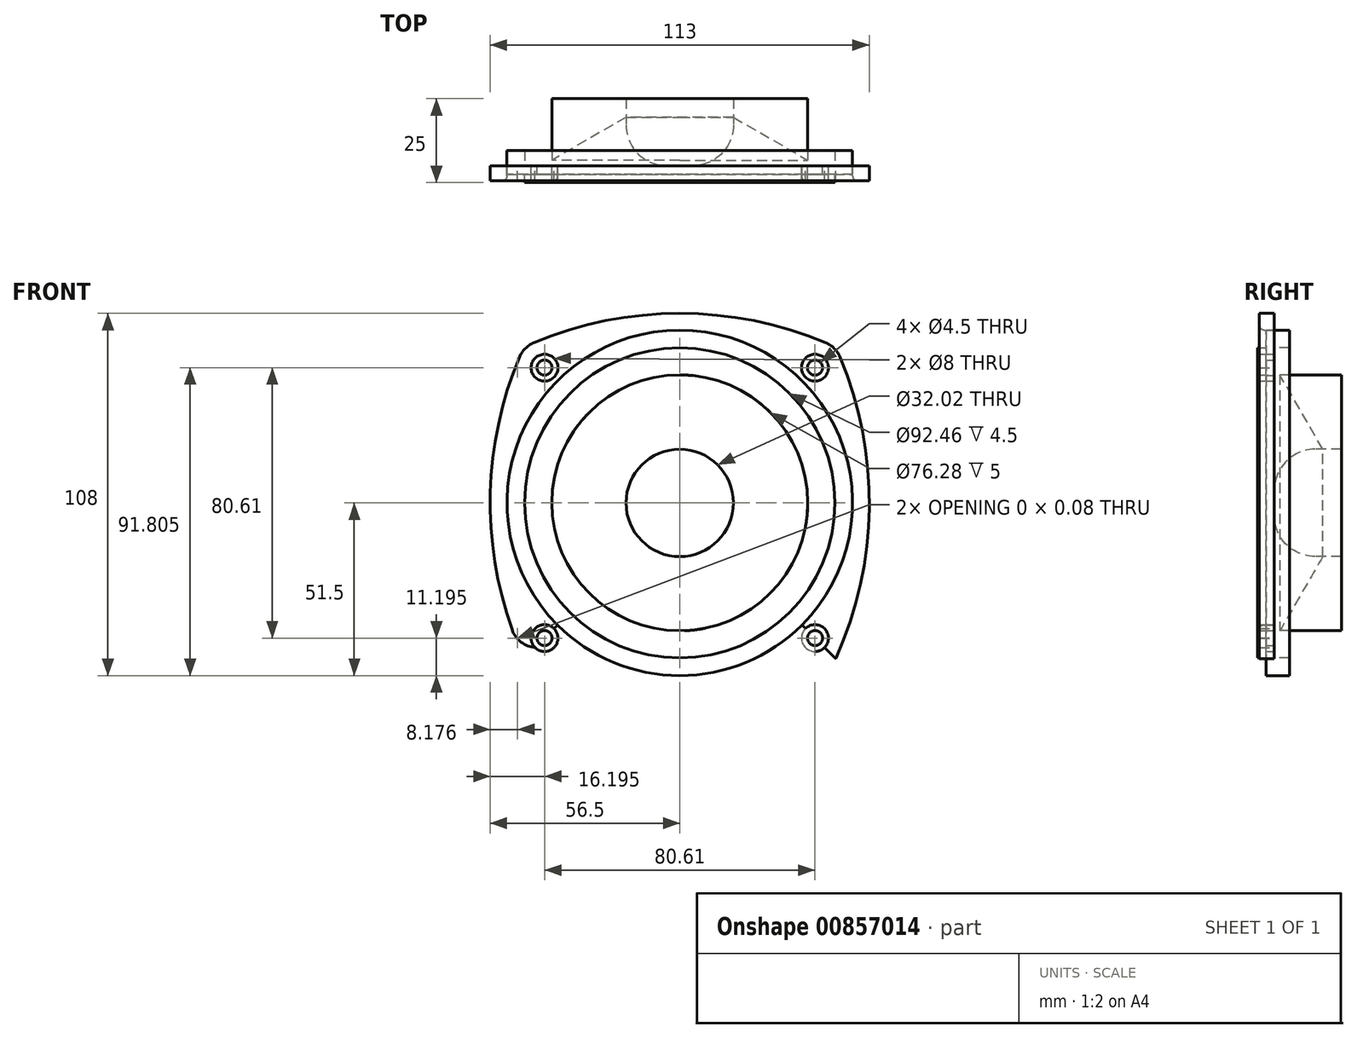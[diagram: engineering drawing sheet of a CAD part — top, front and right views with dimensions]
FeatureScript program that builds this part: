
annotation { "Feature Type Name" : "Feature", "Feature Type Description" : "" }
export const myFeature = defineFeature(function(context is Context, id is Id, definition is map)
    precondition{}
    {
        {
            var Q0;
            Q0=qCreatedBy(makeId("Front.planeOp"),FACE);
            var sketch = newSketch(context, id + "F0", { "sketchPlane" : qUnion([Q0])});
            skCircle(sketch, "E0", {"center": v(0, 0) * mm, "radius": 51.5 * mm});
            skPoint(sketch, "E1", {"position": v(56.5, 0) * mm});
            skPoint(sketch, "E2", {"position": v(-56.5, 0) * mm});
            skPoint(sketch, "E3", {"position": v(43.13, 43.13) * mm});
            skPoint(sketch, "E4", {"position": v(40.3, 40.3) * mm});
            skCircle(sketch, "E5", {"center": v(40.3, 40.3) * mm, "radius": 4 * mm});
            skCircle(sketch, "E6", {"center": v(40.3, 40.3) * mm, "radius": 2.25 * mm});
            skCircle(sketch, "E7.1.0", {"center": v(-40.3, 40.3) * mm, "radius": 4 * mm});
            skCircle(sketch, "E7.1.1", {"center": v(-40.3, 40.3) * mm, "radius": 2.25 * mm});
            skCircle(sketch, "E7.2.0", {"center": v(-40.3, -40.3) * mm, "radius": 4 * mm});
            skCircle(sketch, "E7.2.1", {"center": v(-40.3, -40.3) * mm, "radius": 2.25 * mm});
            skCircle(sketch, "E7.3.0", {"center": v(40.3, -40.3) * mm, "radius": 4 * mm});
            skCircle(sketch, "E7.3.1", {"center": v(40.3, -40.3) * mm, "radius": 2.25 * mm});
            skLineSegment(sketch, "E8", {"start": v(-48.32, 40.34) * mm, "end": v(-48.32, 40.27) * mm});
            skFitSpline(sketch, "E9", {"points": [v(-40.29, -48.3) * mm, v(0, -56.5) * mm, v(40.3, -48.3) * mm], "startDerivative": vector(80.54, -24.59) * mm, "endDerivative": vector(80.6, 24.58) * mm});
            skLineSegment(sketch, "E10.trimOffspring", {"start": v(-48.32, -40.27) * mm, "end": v(-48.32, -40.34) * mm});
            skArc(sketch, "E11.trimOffspring", {"start": v(-48.32, -40.27) * mm, "mid": v(-48.32, -40.3) * mm, "end": v(-48.32, -40.34) * mm});
            skArc(sketch, "E12.1.0", {"start": v(40.27, -48.3) * mm, "mid": v(40.29, -48.3) * mm, "end": v(40.3, -48.3) * mm});
            skArc(sketch, "E12.3.0", {"start": v(-48.32, 40.34) * mm, "mid": v(-48.32, 40.3) * mm, "end": v(-48.32, 40.27) * mm});
            skPoint(sketch, "E13.orphan", {"position": v(-45.98, 45.96) * mm});
            skLineSegment(sketch, "E14.trimOffspring", {"start": v(40.27, -48.3) * mm, "end": v(40.3, -48.3) * mm});
            skPoint(sketch, "E15.start.orphan", {"position": v(45.94, -45.96) * mm});
            skCircle(sketch, "E16", {"center": v(0, 0) * mm, "radius": 46.23 * mm});
            skCircle(sketch, "E17", {"center": v(0, 0) * mm, "radius": 38.14 * mm});
            skCircle(sketch, "E18", {"center": v(0, 0) * mm, "radius": 16 * mm});
            skPoint(sketch, "E19", {"position": v(-46.48, 46.46) * mm});
            skPoint(sketch, "E20.2.0", {"position": v(46.48, -46.46) * mm});
            skPoint(sketch, "E21.1.internal.orphan", {"position": v(-0.02, 56.5) * mm});
            skArc(sketch, "E22.1.0", {"start": v(46.67, -46.67) * mm, "mid": v(46.67, -46.67) * mm, "end": v(46.67, -46.66) * mm});
            skLineSegment(sketch, "E22.anchor1", {"start": v(0, 0) * mm, "end": v(0, -59.19) * mm, "construction": true});
            skLineSegment(sketch, "E22.anchor2", {"start": v(0, 0) * mm, "end": v(0, 59.19) * mm, "construction": true});
            skLineSegment(sketch, "E23", {"start": v(0, 0) * mm, "end": v(-48.98, 48.97) * mm});
            skLineSegment(sketch, "E24", {"start": v(0, 0) * mm, "end": v(50.81, -50.8) * mm});
            skPoint(sketch, "E25.1.0", {"position": v(-46.46, -46.48) * mm});
            skPoint(sketch, "E25.3.0", {"position": v(46.46, 46.48) * mm});
            skArc(sketch, "E26", {"start": v(46.46, 46.48) * mm, "mid": v(-0.01, 56.5) * mm, "end": v(-46.48, 46.46) * mm});
            skArc(sketch, "E27", {"start": v(46.48, -46.46) * mm, "mid": v(56.5, 0.01) * mm, "end": v(46.46, 46.48) * mm});
            skArc(sketch, "E28", {"start": v(-46.48, 46.46) * mm, "mid": v(-56.5, -0.01) * mm, "end": v(-46.46, -46.48) * mm});
            skLineSegment(sketch, "E29", {"start": v(-46.46, -46.48) * mm, "end": v(46.46, 46.48) * mm});
            skArc(sketch, "E30", {"start": v(-46.46, -46.48) * mm, "mid": v(0.01, -56.5) * mm, "end": v(46.48, -46.46) * mm});
            skSolve(sketch);
        }
        {
            var Q0;
            Q0=makeQuery(id+"F0.imprint","IMPRINT",FACE,{"disambiguationData":[TD([[makeQuery(id+"F0.imprint","IMPRINT",EDGE,{"derivedFrom":sQuery(id+"F0.wireOp",EDGE,"E0")}),-1.0]])]});
            var Q1;
            {var subQ13=sQuery(id+"F0.wireOp",EDGE,"E28");Q1=makeQuery(id+"F0.imprint","IMPRINT",FACE,{"disambiguationData":[TD([[makeQuery(id+"F0.imprint","IMPRINT",EDGE,{"derivedFrom":subQ13}),1.0]])]});}
            var Q2;
            {var subQ13=sQuery(id+"F0.wireOp",EDGE,"E27");Q2=makeQuery(id+"F0.imprint","IMPRINT",FACE,{"disambiguationData":[TD([[makeQuery(id+"F0.imprint","IMPRINT",EDGE,{"derivedFrom":subQ13}),1.0]])]});}
            extrude(context, id + "F1", {"entities" : qUnion([Q0, Q1, Q2]), "depth" : 4.5 * mm, "offsetDistance" : 25 * mm});
        }
        {
            var Q0;
            Q0=makeQuery(id+"F1.opExtrude","CAP_EDGE",EDGE,{"disambiguationData":[OSD([sQuery(id+"F0.wireOp",EDGE,"E0")])],"isStart":false});
            fillet(context, id + "F2", {"entities" : qUnion([Q0]), "radius" : 1.5 * mm, "tangentPropagation" : true, "allowEdgeOverflow" : false});
        }
        {
            var Q0;
            Q0=makeQuery(id+"F0.imprint","IMPRINT",FACE,{"disambiguationData":[TD([[makeQuery(id+"F0.imprint","IMPRINT",EDGE,{"derivedFrom":sQuery(id+"F0.wireOp",EDGE,"E0")}),1.0]])]});
            extrude(context, id + "F3", {"entities" : qUnion([Q0]), "oppositeDirection" : true, "depth" : 4.5 * mm, "offsetDistance" : 25 * mm});
        }
        {
            var Q0;
            Q0=makeQuery(id+"F0.imprint","IMPRINT",FACE,{"disambiguationData":[TD([[makeQuery(id+"F0.imprint","IMPRINT",EDGE,{"derivedFrom":sQuery(id+"F0.wireOp",EDGE,"E0")}),1.0]])]});
            extrude(context, id + "F4", {"entities" : qUnion([Q0]), "depth" : 2.5 * mm, "offsetDistance" : 25 * mm});
        }
        {
            var Q0;
            Q0=makeQuery(id+"F0.imprint","IMPRINT",FACE,{"disambiguationData":[TD([[makeQuery(id+"F0.imprint","IMPRINT",EDGE,{"derivedFrom":sQuery(id+"F0.wireOp",EDGE,"E16")}),1.0]])]});
            extrude(context, id + "F5", {"entities" : qUnion([Q0]), "operationType" : NewBodyOperationType.ADD, "depth" : 5 * mm, "offsetDistance" : 25 * mm});
        }
        {
            var Q0;
            Q0=makeQuery(id+"F0.imprint","IMPRINT",FACE,{"disambiguationData":[TD([[makeQuery(id+"F0.imprint","IMPRINT",EDGE,{"derivedFrom":sQuery(id+"F0.wireOp",EDGE,"E17")}),1.0]])]});
            extrude(context, id + "F6", {"entities" : qUnion([Q0]), "oppositeDirection" : true, "depth" : 20 * mm, "offsetDistance" : 25 * mm});
        }
        {
            var Q0;
            Q0=makeQuery(id+"F6.opExtrude","CAP_EDGE",EDGE,{"disambiguationData":[OSD([sQuery(id+"F0.wireOp",EDGE,"E18")])],"isStart":true});
            chamfer(context, id + "F7", {"entities" : qUnion([Q0]), "chamferType" : ChamferType.OFFSET_ANGLE, "width" : 25 * mm, "oppositeDirection" : true, "angle" : 30 * degree});
        }
        {
            var Q0;
            Q0=makeQuery(id+"F0.imprint","IMPRINT",FACE,{"disambiguationData":[TD([[makeQuery(id+"F0.imprint","IMPRINT",EDGE,{"derivedFrom":sQuery(id+"F0.wireOp",EDGE,"E18")}),1.0]])]});
            var Q1;
            {var subQ0=sQuery(id+"F0.wireOp",EDGE,"E29");var subQ1=sQuery(id+"F0.wireOp",EDGE,"E18");var subQ2=makeQuery(id+"F0.imprint","INTERSECT",VERTEX,{"disambiguationData":[OD(0.0)],"derivedFrom":[subQ1,subQ0]});Q1=makeQuery(id+"F0.imprint","IMPRINT",FACE,{"disambiguationData":[TD([[makeQuery(id+"F0.imprint","IMPRINT",EDGE,{"disambiguationData":[TD([[subQ2,1.0]])],"derivedFrom":subQ1}),1.0]])]});}
            var Q2;
            {var subQ0=sQuery(id+"F0.wireOp",EDGE,"E29");var subQ1=sQuery(id+"F0.wireOp",EDGE,"E18");var subQ2=makeQuery(id+"F0.imprint","INTERSECT",VERTEX,{"disambiguationData":[OD(1.0)],"derivedFrom":[subQ1,subQ0]});Q2=makeQuery(id+"F0.imprint","IMPRINT",FACE,{"disambiguationData":[TD([[makeQuery(id+"F0.imprint","IMPRINT",EDGE,{"disambiguationData":[TD([[subQ2,-1.0]])],"derivedFrom":subQ1}),1.0]])]});}
            extrude(context, id + "F8", {"entities" : qUnion([Q0, Q1, Q2]), "oppositeDirection" : true, "depth" : 20 * mm, "offsetDistance" : 25 * mm});
        }
        {
            var Q0;
            {var subQ0=sQuery(id+"F0.wireOp",EDGE,"ajAO1nI6-YHCd-Atq7-Q4zG-g3bYS5PZATk2");var subQ1=sQuery(id+"F0.wireOp",EDGE,"E7.1.0");var subQ2=makeQuery(id+"F0.imprint","INTERSECT",VERTEX,{"disambiguationData":[OD(0.0)],"derivedFrom":[subQ1,subQ0]});Q0=makeQuery(id+"F0.imprint","IMPRINT",FACE,{"disambiguationData":[TD([[makeQuery(id+"F0.imprint","IMPRINT",EDGE,{"disambiguationData":[TD([[subQ2,-1.0]])],"derivedFrom":subQ1}),1.0]])]});}
            var Q1;
            {var subQ0=sQuery(id+"F0.wireOp",EDGE,"ajAO1nI6-YHCd-Atq7-Q4zG-g3bYS5PZATk2");var subQ1=sQuery(id+"F0.wireOp",EDGE,"E7.1.0");var subQ2=makeQuery(id+"F0.imprint","INTERSECT",VERTEX,{"disambiguationData":[OD(0.0)],"derivedFrom":[subQ1,subQ0]});Q1=makeQuery(id+"F0.imprint","IMPRINT",FACE,{"disambiguationData":[TD([[makeQuery(id+"F0.imprint","IMPRINT",EDGE,{"disambiguationData":[TD([[subQ2,1.0]])],"derivedFrom":subQ1}),1.0]])]});}
            var Q2;
            Q2=makeQuery(id+"F0.imprint","IMPRINT",FACE,{"disambiguationData":[TD([[makeQuery(id+"F0.imprint","IMPRINT",EDGE,{"derivedFrom":sQuery(id+"F0.wireOp",EDGE,"E5")}),1.0]])]});
            var Q3;
            Q3=makeQuery(id+"F0.imprint","IMPRINT",FACE,{"disambiguationData":[TD([[makeQuery(id+"F0.imprint","IMPRINT",EDGE,{"derivedFrom":sQuery(id+"F0.wireOp",EDGE,"E7.2.0")}),1.0]])]});
            var Q4;
            {var subQ0=sQuery(id+"F0.wireOp",EDGE,"ajAO1nI6-YHCd-Atq7-Q4zG-g3bYS5PZATk2");var subQ1=sQuery(id+"F0.wireOp",EDGE,"E7.3.0");var subQ2=makeQuery(id+"F0.imprint","INTERSECT",VERTEX,{"disambiguationData":[OD(0.0)],"derivedFrom":[subQ1,subQ0]});Q4=makeQuery(id+"F0.imprint","IMPRINT",FACE,{"disambiguationData":[TD([[makeQuery(id+"F0.imprint","IMPRINT",EDGE,{"disambiguationData":[TD([[subQ2,-1.0]])],"derivedFrom":subQ1}),1.0]])]});}
            var Q5;
            {var subQ0=sQuery(id+"F0.wireOp",EDGE,"ajAO1nI6-YHCd-Atq7-Q4zG-g3bYS5PZATk2");var subQ1=sQuery(id+"F0.wireOp",EDGE,"E7.3.0");var subQ2=makeQuery(id+"F0.imprint","INTERSECT",VERTEX,{"disambiguationData":[OD(0.0)],"derivedFrom":[subQ1,subQ0]});Q5=makeQuery(id+"F0.imprint","IMPRINT",FACE,{"disambiguationData":[TD([[makeQuery(id+"F0.imprint","IMPRINT",EDGE,{"disambiguationData":[TD([[subQ2,1.0]])],"derivedFrom":subQ1}),1.0]])]});}
            extrude(context, id + "F9", {"entities" : qUnion([Q0, Q1, Q2, Q3, Q4, Q5]), "depth" : 2.5 * mm, "offsetDistance" : 25 * mm});
        }
        {
            var Q0;
            Q0=makeQuery(id+"F8.opExtrude","CAP_EDGE",EDGE,{"disambiguationData":[OSD([sQuery(id+"F0.wireOp",EDGE,"E18")])],"isStart":true});
            fillet(context, id + "F10", {"entities" : qUnion([Q0]), "radius" : 12.2 * mm, "tangentPropagation" : true, "allowEdgeOverflow" : false});
        }
        {
            var Q0;
            Q0=makeQuery(id+"F1.opExtrude","SWEPT_EDGE",EDGE,{"disambiguationData":[OSD([sQuery(id+"F0.wireOp",EDGE,"E26"),sQuery(id+"F0.wireOp",EDGE,"E28")])]});
            var Q1;
            Q1=makeQuery(id+"F1.opExtrude","SWEPT_EDGE",EDGE,{"disambiguationData":[OSD([sQuery(id+"F0.wireOp",EDGE,"E26"),sQuery(id+"F0.wireOp",EDGE,"E27"),sQuery(id+"F0.wireOp",EDGE,"E29")])]});
            var Q2;
            Q2=makeQuery(id+"F1.opExtrude","SWEPT_EDGE",EDGE,{"disambiguationData":[OSD([sQuery(id+"F0.wireOp",EDGE,"E27"),sQuery(id+"F0.wireOp",EDGE,"E30")])]});
            var Q3;
            Q3=makeQuery(id+"F1.opExtrude","SWEPT_EDGE",EDGE,{"disambiguationData":[OSD([sQuery(id+"F0.wireOp",EDGE,"E28"),sQuery(id+"F0.wireOp",EDGE,"E29"),sQuery(id+"F0.wireOp",EDGE,"E30")])]});
            fillet(context, id + "F11", {"entities" : qUnion([Q0, Q1, Q2, Q3]), "radius" : 8 * mm, "tangentPropagation" : true, "allowEdgeOverflow" : false});
        }
    });
